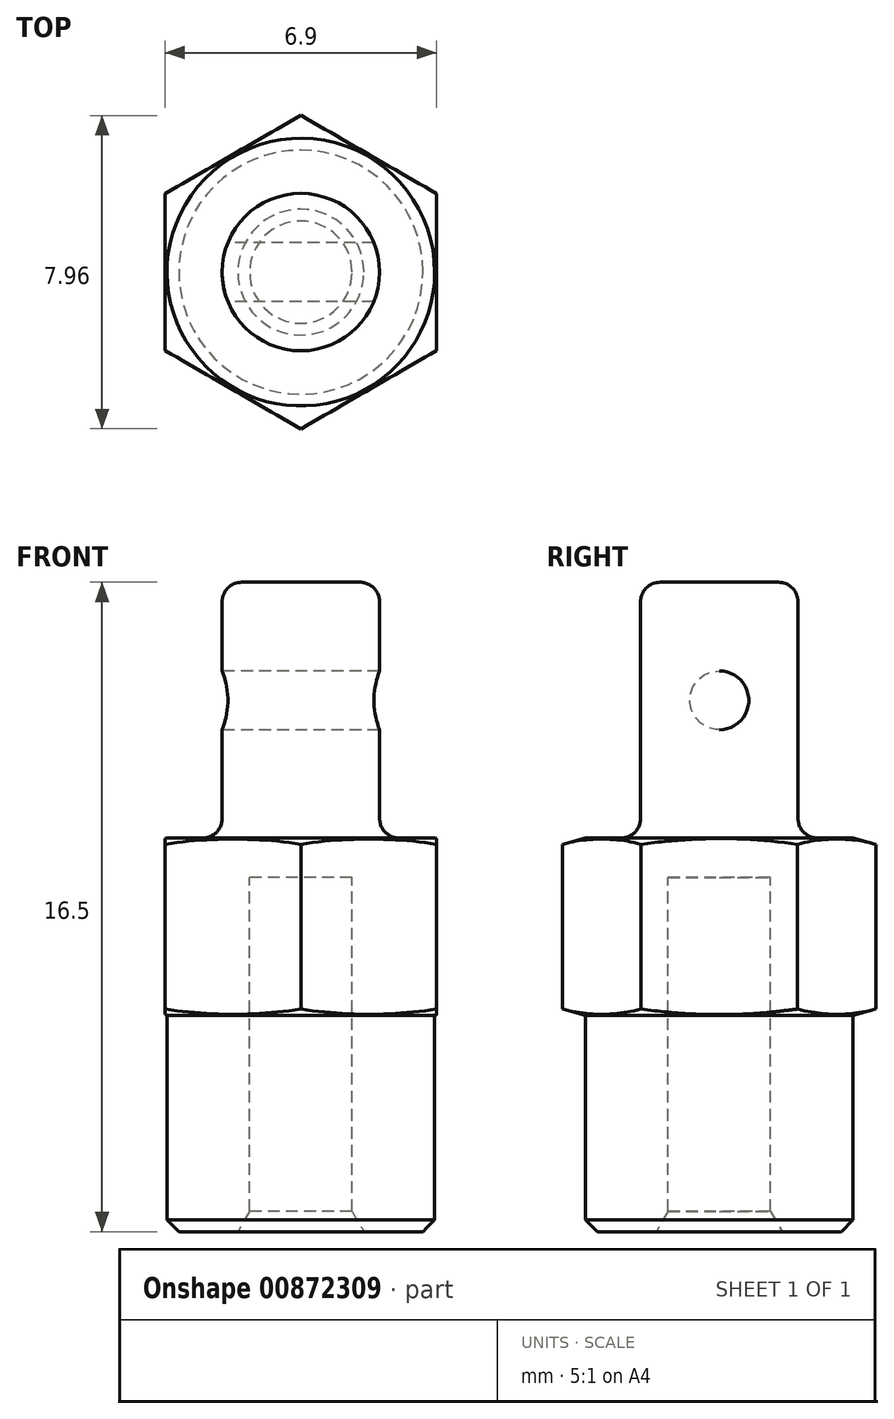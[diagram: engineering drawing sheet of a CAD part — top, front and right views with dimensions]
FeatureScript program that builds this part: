
annotation { "Feature Type Name" : "Feature", "Feature Type Description" : "" }
export const myFeature = defineFeature(function(context is Context, id is Id, definition is map)
    precondition{}
    {
        {
            var Q0;
            Q0=qCreatedBy(makeId("Front.planeOp"),FACE);
            var sketch = newSketch(context, id + "F0", { "sketchPlane" : qUnion([Q0])});
            skLineSegment(sketch, "E0", {"start": v(1.3, 0) * mm, "end": v(3.4, 0) * mm});
            skLineSegment(sketch, "E1", {"start": v(3.4, 0) * mm, "end": v(3.4, 5.5) * mm});
            skLineSegment(sketch, "E2", {"start": v(3.4, 5.5) * mm, "end": v(4, 5.66) * mm});
            skLineSegment(sketch, "E3", {"start": v(4, 5.66) * mm, "end": v(4, 9.84) * mm});
            skLineSegment(sketch, "E4", {"start": v(4, 9.84) * mm, "end": v(3.4, 10) * mm});
            skLineSegment(sketch, "E5", {"start": v(3.4, 10) * mm, "end": v(2.5, 10) * mm});
            skLineSegment(sketch, "E6", {"start": v(2, 10.5) * mm, "end": v(2, 16) * mm});
            skLineSegment(sketch, "E7", {"start": v(1.5, 16.5) * mm, "end": v(0, 16.5) * mm});
            skPoint(sketch, "E8.visualSharp", {"position": v(2, 16.5) * mm});
            skArc(sketch, "E8.filletArc", {"start": v(2, 16) * mm, "mid": v(1.85, 16.35) * mm, "end": v(1.5, 16.5) * mm});
            skPoint(sketch, "E9.visualSharp", {"position": v(2, 10) * mm});
            skArc(sketch, "E9.filletArc", {"start": v(2, 10.5) * mm, "mid": v(2.15, 10.15) * mm, "end": v(2.5, 10) * mm});
            skLineSegment(sketch, "E10", {"start": v(0, 9) * mm, "end": v(1.3, 9) * mm});
            skLineSegment(sketch, "E11", {"start": v(1.3, 9) * mm, "end": v(1.3, 0) * mm});
            skLineSegment(sketch, "E12", {"start": v(0, 23.26) * mm, "end": v(0, -7.72) * mm, "construction": true});
            skLineSegment(sketch, "E13", {"start": v(0, 16.5) * mm, "end": v(0, 9) * mm});
            skSolve(sketch);
        }
        {
            var Q0;
            Q0 = qSketchRegion(id + "F0", true);
            var Q1;
            Q1=sQuery(id+"F0.wireOp",EDGE,"E12");
            revolve(context, id + "F1", {"surfaceOperationType" : NewSurfaceOperationType.NEW, "entities" : qUnion([Q0]), "axis" : qUnion([Q1]), "revolveType" : RevolveType.FULL});
        }
        {
            var Q0;
            Q0=qCreatedBy(makeId("Top.planeOp"),FACE);
            var sketch = newSketch(context, id + "F2", { "sketchPlane" : qUnion([Q0])});
            skCircle(sketch, "E14.cCircle", {"center": v(0, 0) * mm, "radius": 3.45 * mm, "construction": true});
            skLineSegment(sketch, "E14.0", {"start": v(3.45, 2) * mm, "end": v(3.45, -2) * mm});
            skLineSegment(sketch, "E14.1", {"start": v(3.45, -2) * mm, "end": v(0, -3.98) * mm});
            skLineSegment(sketch, "E14.2", {"start": v(0, -3.98) * mm, "end": v(-3.45, -2) * mm});
            skLineSegment(sketch, "E14.3", {"start": v(-3.45, -2) * mm, "end": v(-3.45, 2) * mm});
            skLineSegment(sketch, "E14.4", {"start": v(-3.45, 2) * mm, "end": v(0, 3.98) * mm});
            skLineSegment(sketch, "E14.5", {"start": v(0, 3.98) * mm, "end": v(3.45, 2) * mm});
            skPoint(sketch, "E14.0.midPoint", {"position": v(3.45, 0) * mm});
            skCircle(sketch, "E15", {"center": v(0, -0.62) * mm, "radius": 5.94 * mm});
            skSolve(sketch);
        }
        {
            var Q0;
            Q0 = qSketchRegion(id + "F2", true);
            extrude(context, id + "F3", {"entities" : qUnion([Q0]), "operationType" : NewBodyOperationType.REMOVE, "endBound" : BoundingType.THROUGH_ALL, "depth" : 25 * mm, "offsetDistance" : 25 * mm});
        }
        {
            var Q0;
            Q0=qCreatedBy(makeId("Right.planeOp"),FACE);
            var sketch = newSketch(context, id + "F4", { "sketchPlane" : qUnion([Q0])});
            skCircle(sketch, "E16", {"center": v(0, 13.5) * mm, "radius": 0.75 * mm});
            skSolve(sketch);
        }
        {
            var Q0;
            Q0 = qSketchRegion(id + "F4", true);
            extrude(context, id + "F5", {"entities" : qUnion([Q0]), "operationType" : NewBodyOperationType.REMOVE, "endBound" : BoundingType.THROUGH_ALL, "depth" : 25 * mm, "offsetDistance" : 25 * mm, "hasSecondDirection" : true, "secondDirectionBound" : SecondDirectionBoundingType.THROUGH_ALL, "secondDirectionOppositeDirection" : true, "secondDirectionDepth" : 25 * mm});
        }
        {
            var Q0;
            Q0=makeQuery(id+"F1.opRevolve","SWEPT_EDGE",EDGE,{"disambiguationData":[OSD([sQuery(id+"F0.wireOp",EDGE,"E0"),sQuery(id+"F0.wireOp",EDGE,"E1")])]});
            chamfer(context, id + "F6", {"entities" : qUnion([Q0]), "width" : 0.3 * mm, "tangentPropagation" : true});
        }
        {
            var Q0;
            Q0=makeQuery(id+"F1.opRevolve","SWEPT_EDGE",EDGE,{"disambiguationData":[OSD([sQuery(id+"F0.wireOp",EDGE,"E0"),sQuery(id+"F0.wireOp",EDGE,"E11")])]});
            chamfer(context, id + "F7", {"entities" : qUnion([Q0]), "chamferType" : ChamferType.OFFSET_ANGLE, "width" : 0.3 * mm, "oppositeDirection" : false, "angle" : 60 * degree, "tangentPropagation" : true});
        }
    });
